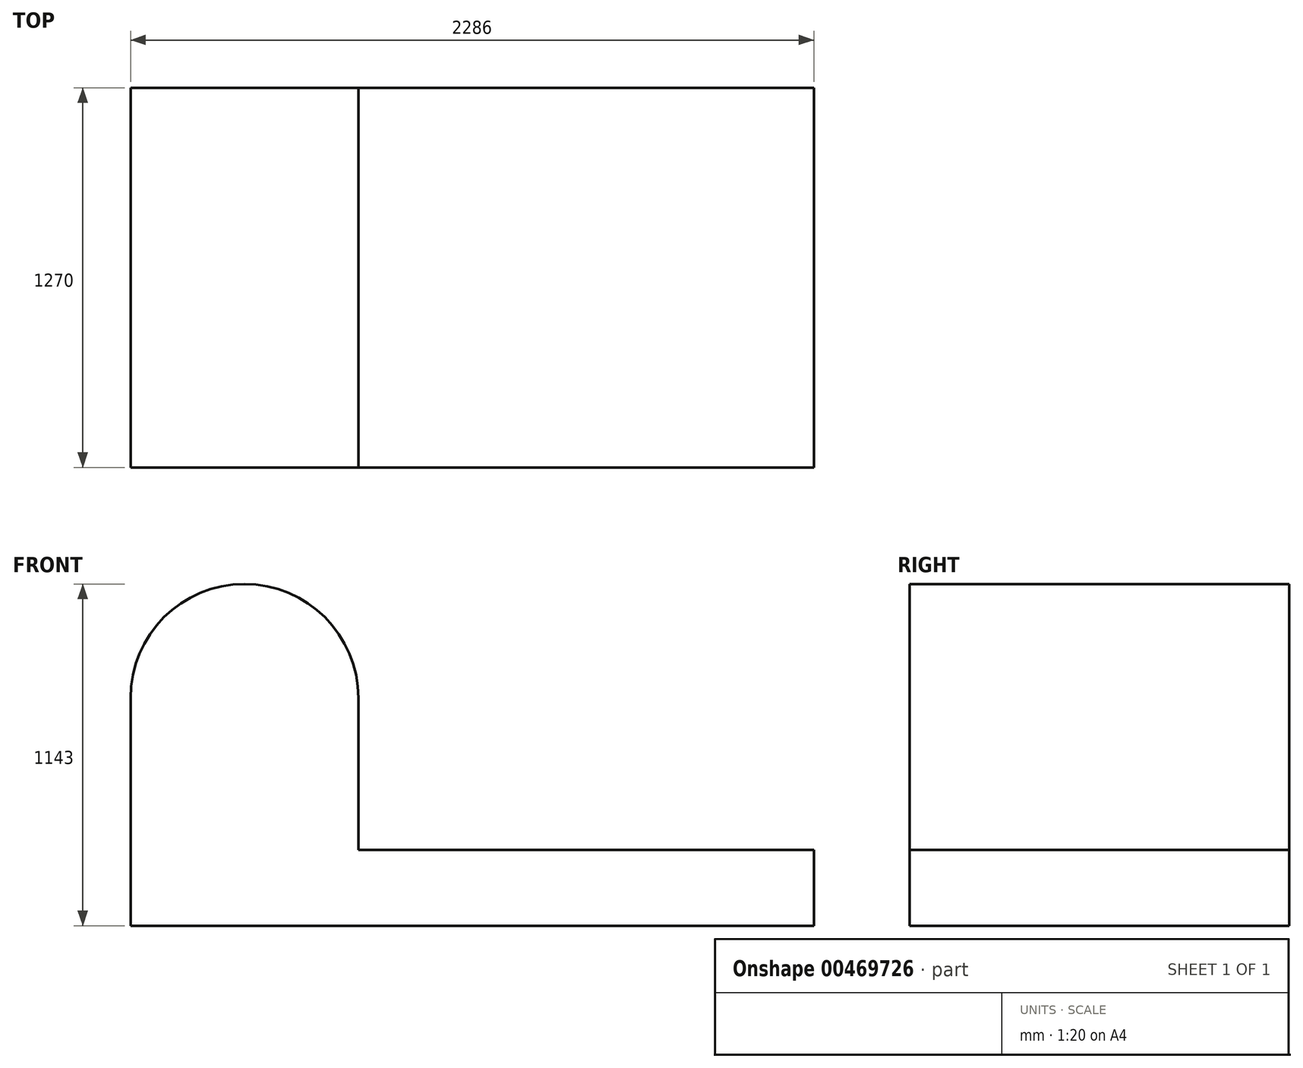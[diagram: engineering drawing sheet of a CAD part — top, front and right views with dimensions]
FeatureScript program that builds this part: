
annotation { "Feature Type Name" : "Feature", "Feature Type Description" : "" }
export const myFeature = defineFeature(function(context is Context, id is Id, definition is map)
    precondition{}
    {
        {
            var Q0;
            Q0=qCreatedBy(makeId("Front.planeOp"),FACE);
            var sketch = newSketch(context, id + "F0", { "sketchPlane" : qUnion([Q0])});
            skLineSegment(sketch, "E0.bottom", {"start": v(0, 0) * mm, "end": v(-762, 0) * mm});
            skLineSegment(sketch, "E0.left", {"start": v(0, 254) * mm, "end": v(0, 762) * mm});
            skLineSegment(sketch, "E0.right", {"start": v(-762, 0) * mm, "end": v(-762, 762) * mm});
            skLineSegment(sketch, "E1.bottom", {"start": v(-762, 0) * mm, "end": v(1524, 0) * mm});
            skLineSegment(sketch, "E1.top", {"start": v(0, 254) * mm, "end": v(1524, 254) * mm});
            skLineSegment(sketch, "E1.left", {"start": v(-762, 0) * mm, "end": v(-762, 254) * mm});
            skLineSegment(sketch, "E1.right", {"start": v(1524, 0) * mm, "end": v(1524, 254) * mm});
            skArc(sketch, "E2", {"start": v(0, 762) * mm, "mid": v(-381, 1143) * mm, "end": v(-762, 762) * mm});
            skSolve(sketch);
        }
        {
            var Q0;
            Q0 = qSketchRegion(id + "F0", true);
            extrude(context, id + "F1", {"entities" : qUnion([Q0]), "endBound" : BoundingType.SYMMETRIC, "depth" : 1270 * mm});
        }
    });
